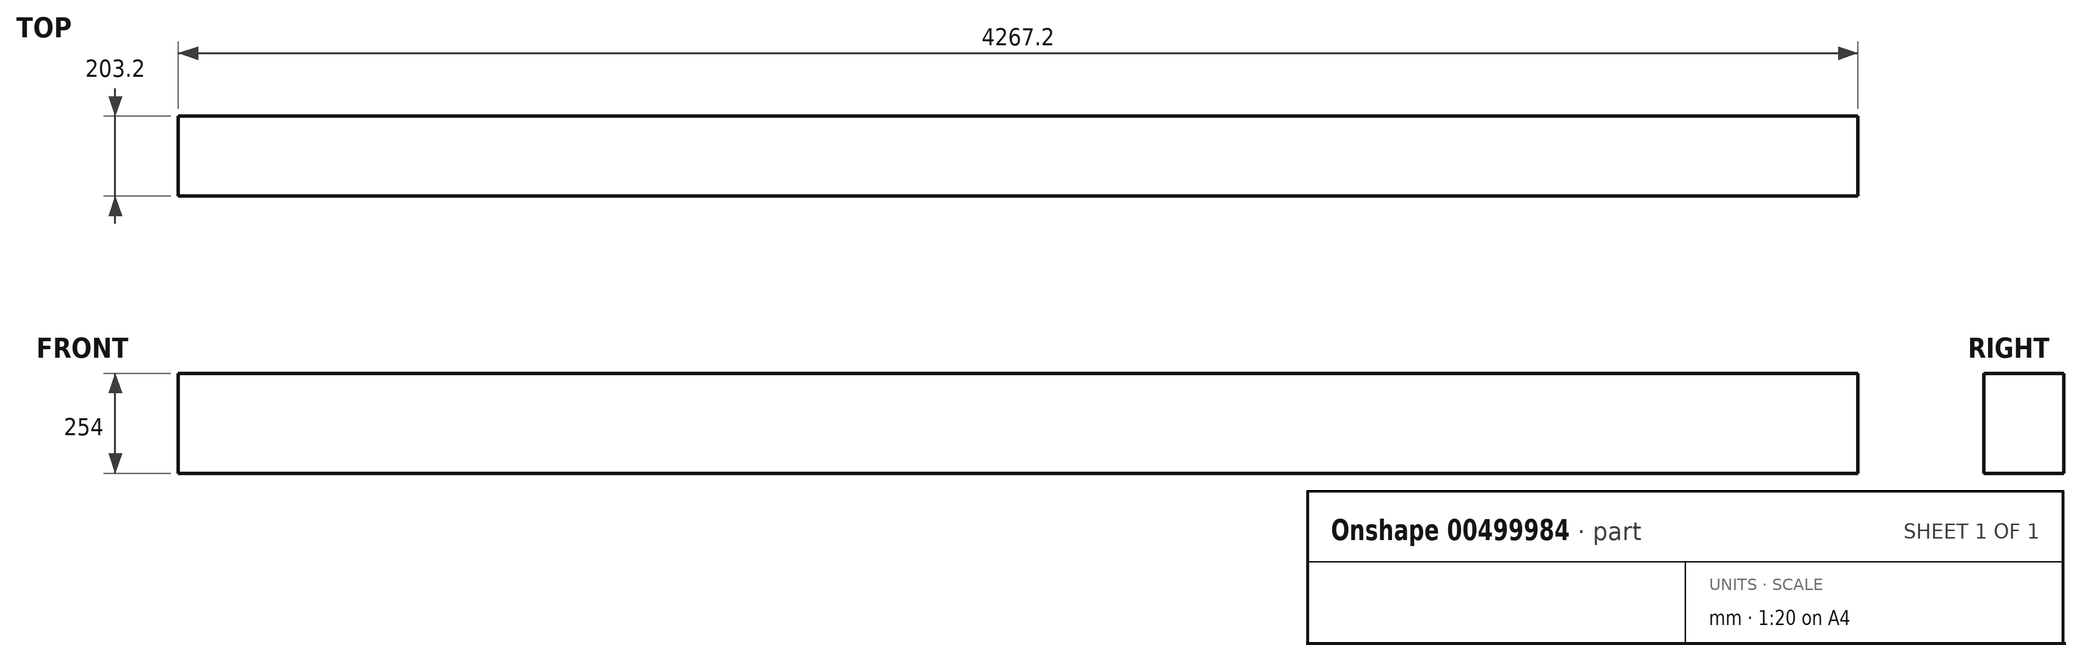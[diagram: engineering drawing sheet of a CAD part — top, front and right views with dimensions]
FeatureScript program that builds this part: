
annotation { "Feature Type Name" : "Feature", "Feature Type Description" : "" }
export const myFeature = defineFeature(function(context is Context, id is Id, definition is map)
    precondition{}
    {
        {
            var Q0;
            Q0=qCreatedBy(makeId("Front.planeOp"), FACE);
            var sketch = newSketch(context, id + "F0", { "sketchPlane" : qUnion([Q0])});
            skLineSegment(sketch, "E0.bottom", {"start": v(0, 0) * mm, "end": v(-4267.2, 0) * mm});
            skLineSegment(sketch, "E0.top", {"start": v(0, 254) * mm, "end": v(-4267.2, 254) * mm});
            skLineSegment(sketch, "E0.left", {"start": v(0, 0) * mm, "end": v(0, 254) * mm});
            skLineSegment(sketch, "E0.right", {"start": v(-4267.2, 0) * mm, "end": v(-4267.2, 254) * mm});
            skSolve(sketch);
        }
        {
            var Q0;
            Q0 = qSketchRegion(id + "F0", true);
            extrude(context, id + "F1", {"entities" : qUnion([Q0]), "depth" : 203.2 * mm, "offsetDistance" : 25.4 * mm});
        }
    });
